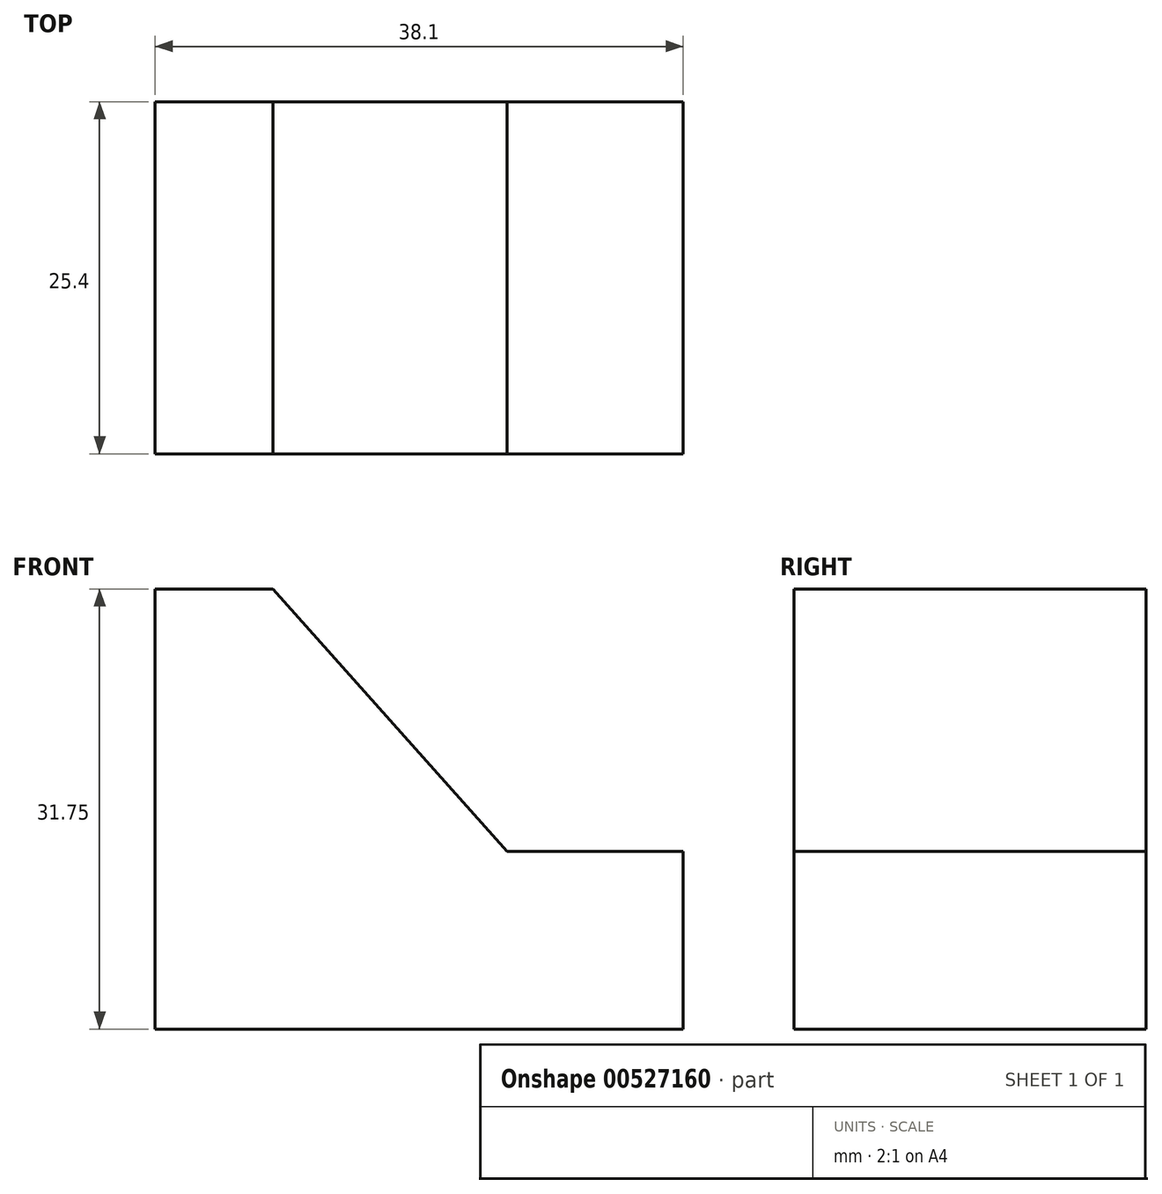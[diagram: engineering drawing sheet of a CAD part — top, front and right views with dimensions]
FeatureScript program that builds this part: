
annotation { "Feature Type Name" : "Feature", "Feature Type Description" : "" }
export const myFeature = defineFeature(function(context is Context, id is Id, definition is map)
    precondition{}
    {
        {
            var Q0;
            Q0=qCreatedBy(makeId("Front.planeOp"),FACE);
            var sketch = newSketch(context, id + "F0", { "sketchPlane" : qUnion([Q0])});
            skLineSegment(sketch, "E0", {"start": v(-38.1, 0) * mm, "end": v(-38.1, 31.75) * mm});
            skLineSegment(sketch, "E1", {"start": v(0, 0) * mm, "end": v(0, 31.75) * mm});
            skLineSegment(sketch, "E2", {"start": v(-38.1, 31.75) * mm, "end": v(0, 31.75) * mm});
            skLineSegment(sketch, "E3", {"start": v(-38.1, 0) * mm, "end": v(0, 0) * mm});
            skSolve(sketch);
        }
        {
            var Q0;
            Q0=makeQuery(id+"F0.imprint","IMPRINT",FACE,{"disambiguationData":[TD([[makeQuery(id+"F0.imprint","IMPRINT",EDGE,{"derivedFrom":sQuery(id+"F0.wireOp",EDGE,"E0")}),-1.0]])]});
            extrude(context, id + "F1", {"entities" : qUnion([Q0]), "depth" : 25.4 * mm, "offsetDistance" : 25.4 * mm});
        }
        {
            var Q0;
            Q0=makeQuery(id+"F1.opExtrude","CAP_FACE",FACE,{"disambiguationData":[OSD([sQuery(id+"F0.wireOp",EDGE,"E0"),sQuery(id+"F0.wireOp",EDGE,"E1"),sQuery(id+"F0.wireOp",EDGE,"E2"),sQuery(id+"F0.wireOp",EDGE,"E3")])],"isStart":false});
            var sketch = newSketch(context, id + "F2", { "sketchPlane" : qUnion([Q0])});
            skLineSegment(sketch, "E4", {"start": v(-29.62, 31.75) * mm, "end": v(-12.7, 12.8) * mm});
            skLineSegment(sketch, "E5", {"start": v(-12.7, 12.8) * mm, "end": v(0, 12.8) * mm});
            skSolve(sketch);
        }
        {
            var Q0;
            {var subQ0=sQuery(id+"F2.wireOp",EDGE,"E4");Q0=makeQuery(id+"F2.imprint","IMPRINT",FACE,{"disambiguationData":[TD([[makeQuery(id+"F2.imprint","IMPRINT",EDGE,{"derivedFrom":subQ0}),1.0]])]});}
            extrude(context, id + "F3", {"entities" : qUnion([Q0]), "operationType" : NewBodyOperationType.REMOVE, "oppositeDirection" : true, "depth" : 25.4 * mm, "offsetDistance" : 25.4 * mm});
        }
    });
